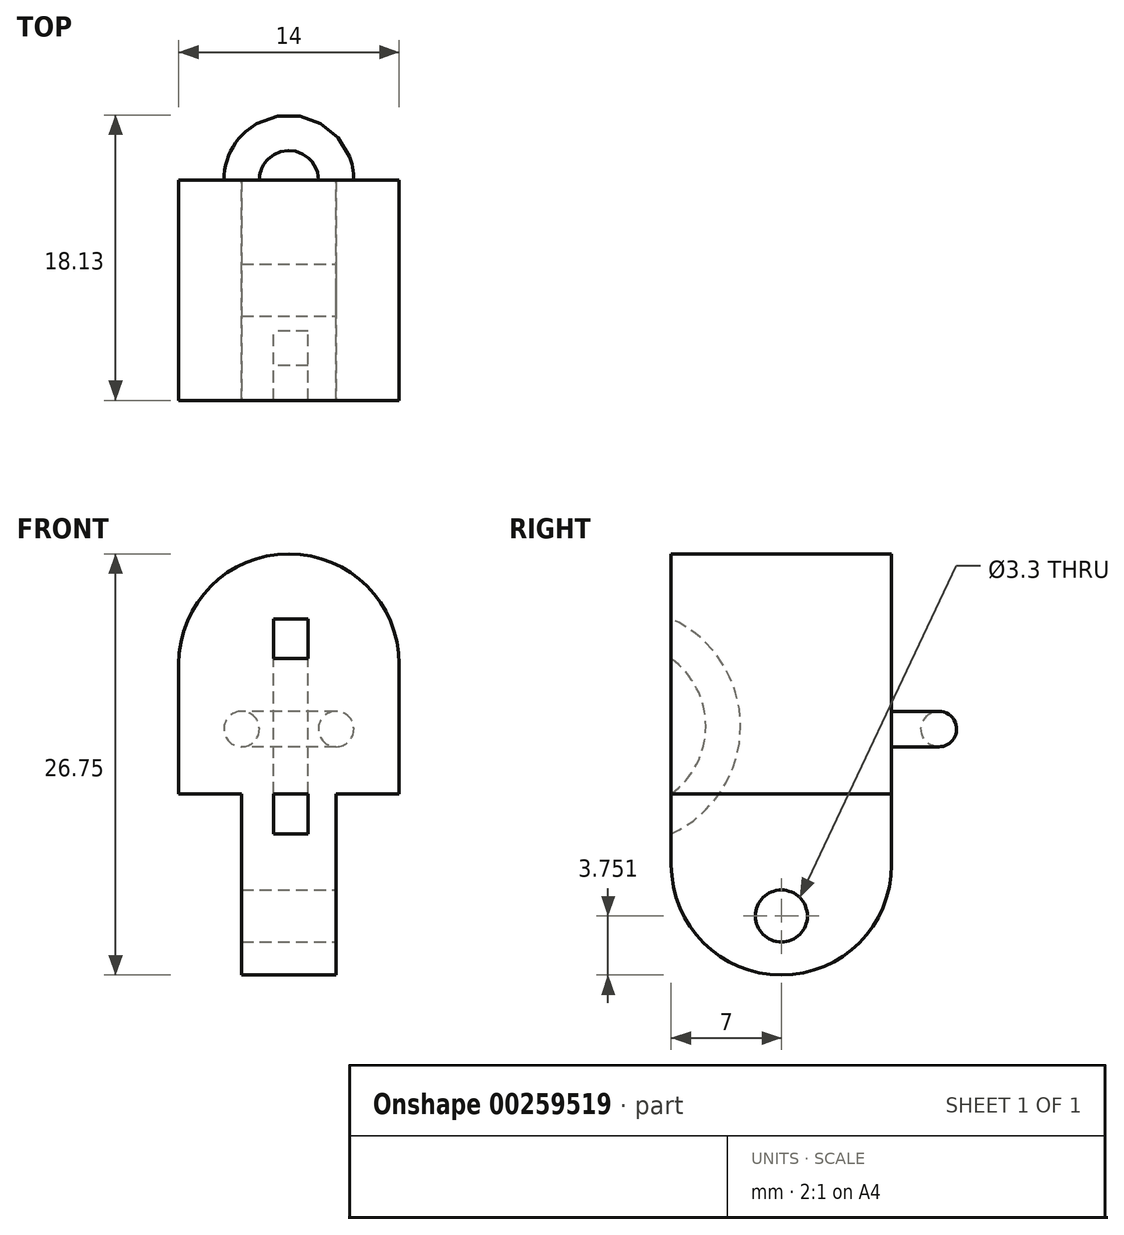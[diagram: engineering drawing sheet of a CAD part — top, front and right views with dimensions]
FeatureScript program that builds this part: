
annotation { "Feature Type Name" : "Feature", "Feature Type Description" : "" }
export const myFeature = defineFeature(function(context is Context, id is Id, definition is map)
    precondition{}
    {
        {
            var Q0;
            Q0=qCreatedBy(makeId("Front.planeOp"),FACE);
            var sketch = newSketch(context, id + "F0", { "sketchPlane" : qUnion([Q0])});
            skLineSegment(sketch, "E0.left", {"start": v(-38.61, 31.27) * mm, "end": v(-38.61, 23.02) * mm});
            skLineSegment(sketch, "E0.right", {"start": v(-24.61, 31.27) * mm, "end": v(-24.61, 23.02) * mm});
            skArc(sketch, "E1", {"start": v(-24.61, 31.27) * mm, "mid": v(-31.61, 38.27) * mm, "end": v(-38.61, 31.27) * mm});
            skLineSegment(sketch, "E2", {"start": v(-34.61, 19.02) * mm, "end": v(-34.61, 11.52) * mm});
            skLineSegment(sketch, "E3", {"start": v(-34.61, 11.52) * mm, "end": v(-28.61, 11.52) * mm});
            skLineSegment(sketch, "E4", {"start": v(-28.61, 11.52) * mm, "end": v(-28.61, 19.02) * mm});
            skLineSegment(sketch, "E5", {"start": v(-28.61, 11.52) * mm, "end": v(-28.61, 15.27) * mm});
            skPoint(sketch, "E6", {"position": v(-31.61, 38.27) * mm});
            skLineSegment(sketch, "E7", {"start": v(-34.61, 19.02) * mm, "end": v(-34.61, 22.02) * mm});
            skLineSegment(sketch, "E8", {"start": v(-28.61, 19.02) * mm, "end": v(-28.61, 22.02) * mm});
            skLineSegment(sketch, "E9", {"start": v(-34.61, 22.02) * mm, "end": v(-34.61, 23.02) * mm});
            skLineSegment(sketch, "E10", {"start": v(-34.61, 23.02) * mm, "end": v(-38.61, 23.02) * mm});
            skLineSegment(sketch, "E11", {"start": v(-28.61, 22.02) * mm, "end": v(-28.61, 23.02) * mm});
            skLineSegment(sketch, "E12", {"start": v(-28.61, 23.02) * mm, "end": v(-24.61, 23.02) * mm});
            skSolve(sketch);
        }
        {
            var Q0;
            Q0 = qSketchRegion(id + "F0", true);
            extrude(context, id + "F1", {"entities" : qUnion([Q0]), "depth" : 14 * mm});
        }
        {
            var Q0;
            Q0=makeQuery(id+"F1.opExtrude","SWEPT_FACE",FACE,{"disambiguationData":[OSD([sQuery(id+"F0.wireOp",EDGE,"E4")])]});
            var sketch = newSketch(context, id + "F2", { "sketchPlane" : qUnion([Q0])});
            skCircle(sketch, "E13", {"center": v(-7, 15.27) * mm, "radius": 1.65 * mm});
            skSolve(sketch);
        }
        {
            var Q0;
            Q0 = qSketchRegion(id + "F2", true);
            extrude(context, id + "F3", {"entities" : qUnion([Q0]), "operationType" : NewBodyOperationType.REMOVE, "oppositeDirection" : true, "depth" : 25 * mm});
        }
        {
            var Q0;
            Q0=makeQuery(id+"F1.opExtrude","CAP_EDGE",EDGE,{"disambiguationData":[OSD([sQuery(id+"F0.wireOp",EDGE,"E3")])],"isStart":false});
            var Q1;
            Q1=makeQuery(id+"F1.opExtrude","CAP_EDGE",EDGE,{"disambiguationData":[OSD([sQuery(id+"F0.wireOp",EDGE,"E3")])],"isStart":true});
            fillet(context, id + "F4", {"entities" : qUnion([Q0, Q1]), "radius" : 7 * mm, "tangentPropagation" : true, "allowEdgeOverflow" : false});
        }
        {
            var Q0;
            Q0=makeQuery(id+"F1.opExtrude","CAP_FACE",FACE,{"disambiguationData":[OSD([sQuery(id+"F0.wireOp",EDGE,"E0.left"),sQuery(id+"F0.wireOp",EDGE,"E0.right"),sQuery(id+"F0.wireOp",EDGE,"E1"),sQuery(id+"F0.wireOp",EDGE,"E2"),sQuery(id+"F0.wireOp",EDGE,"E3"),sQuery(id+"F0.wireOp",EDGE,"E4"),sQuery(id+"F0.wireOp",EDGE,"E5"),sQuery(id+"F0.wireOp",EDGE,"E7"),sQuery(id+"F0.wireOp",EDGE,"E8"),sQuery(id+"F0.wireOp",EDGE,"E9"),sQuery(id+"F0.wireOp",EDGE,"E10"),sQuery(id+"F0.wireOp",EDGE,"E11"),sQuery(id+"F0.wireOp",EDGE,"E12")])],"isStart":false});
            var sketch = newSketch(context, id + "F5", { "sketchPlane" : qUnion([Q0])});
            skLineSegment(sketch, "E14", {"start": v(-31.61, 38.27) * mm, "end": v(-31.61, 18.52) * mm});
            skCircle(sketch, "E15", {"center": v(-34.61, 27.15) * mm, "radius": 1.13 * mm});
            skPoint(sketch, "E16.orphan", {"position": v(-24.61, 27.15) * mm});
            skPoint(sketch, "E17.orphan", {"position": v(-31.61, 27.15) * mm});
            skPoint(sketch, "E18.start.orphan", {"position": v(-38.61, 27.15) * mm});
            skSolve(sketch);
        }
        {
            var Q0;
            Q0=makeQuery(id+"F5.imprint","IMPRINT",FACE,{"disambiguationData":[TD([[makeQuery(id+"F5.imprint","IMPRINT",EDGE,{"derivedFrom":sQuery(id+"F5.wireOp",EDGE,"E15")}),1.0]])]});
            var Q1;
            Q1=sQuery(id+"F5.wireOp",EDGE,"E14");
            revolve(context, id + "F6", {"operationType" : NewBodyOperationType.ADD, "entities" : qUnion([Q0]), "axis" : qUnion([Q1]), "revolveType" : RevolveType.FULL});
        }
        {
            var Q0;
            Q0=makeQuery(id+"F1.opExtrude","CAP_FACE",FACE,{"disambiguationData":[OSD([sQuery(id+"F0.wireOp",EDGE,"E0.left"),sQuery(id+"F0.wireOp",EDGE,"E0.right"),sQuery(id+"F0.wireOp",EDGE,"E1"),sQuery(id+"F0.wireOp",EDGE,"E2"),sQuery(id+"F0.wireOp",EDGE,"E3"),sQuery(id+"F0.wireOp",EDGE,"E4"),sQuery(id+"F0.wireOp",EDGE,"E5"),sQuery(id+"F0.wireOp",EDGE,"E7"),sQuery(id+"F0.wireOp",EDGE,"E8"),sQuery(id+"F0.wireOp",EDGE,"E9"),sQuery(id+"F0.wireOp",EDGE,"E10"),sQuery(id+"F0.wireOp",EDGE,"E11"),sQuery(id+"F0.wireOp",EDGE,"E12")])],"isStart":true});
            var sketch = newSketch(context, id + "F7", { "sketchPlane" : qUnion([Q0])});
            skLineSegment(sketch, "E19", {"start": v(31.61, 38.27) * mm, "end": v(31.61, 18.52) * mm});
            skPoint(sketch, "E20.orphan", {"position": v(38.61, 27.15) * mm});
            skPoint(sketch, "E21.orphan", {"position": v(24.61, 27.15) * mm});
            skCircle(sketch, "E22", {"center": v(28.61, 27.15) * mm, "radius": 1.13 * mm});
            skPoint(sketch, "E23.orphan", {"position": v(31.61, 27.15) * mm});
            skSolve(sketch);
        }
        {
            var Q0;
            Q0=makeQuery(id+"F7.imprint","IMPRINT",FACE,{"disambiguationData":[TD([[makeQuery(id+"F7.imprint","IMPRINT",EDGE,{"derivedFrom":sQuery(id+"F7.wireOp",EDGE,"E22")}),1.0]])]});
            var Q1;
            Q1=sQuery(id+"F7.wireOp",EDGE,"E19");
            revolve(context, id + "F8", {"operationType" : NewBodyOperationType.ADD, "entities" : qUnion([Q0]), "axis" : qUnion([Q1]), "revolveType" : RevolveType.FULL});
        }
        {
            var Q0;
            Q0=qCreatedBy(makeId("Top.planeOp"),FACE);
            var sketch = newSketch(context, id + "F9", { "sketchPlane" : qUnion([Q0])});
            skLineSegment(sketch, "E24.0.0", {"start": v(-24.61, 0) * mm, "end": v(-38.61, 0) * mm});
            skLineSegment(sketch, "E24.0.1", {"start": v(-38.61, 0) * mm, "end": v(-38.61, -14) * mm});
            skLineSegment(sketch, "E24.0.2", {"start": v(-38.61, -14) * mm, "end": v(-24.61, -14) * mm});
            skLineSegment(sketch, "E24.0.3", {"start": v(-24.61, -14) * mm, "end": v(-24.61, 0) * mm});
            skLineSegment(sketch, "E25.top", {"start": v(-38.61, -20.43) * mm, "end": v(-24.61, -20.43) * mm});
            skLineSegment(sketch, "E25.left", {"start": v(-38.61, -14) * mm, "end": v(-38.61, -20.43) * mm});
            skLineSegment(sketch, "E25.right", {"start": v(-24.61, -14) * mm, "end": v(-24.61, -20.43) * mm});
            skSolve(sketch);
        }
        {
            var Q0;
            Q0=makeQuery(id+"F9.imprint","IMPRINT",FACE,{"disambiguationData":[TD([[makeQuery(id+"F9.imprint","IMPRINT",EDGE,{"derivedFrom":sQuery(id+"F9.wireOp",EDGE,"E24.0.2")}),-1.0]])]});
            extrude(context, id + "F10", {"entities" : qUnion([Q0]), "operationType" : NewBodyOperationType.REMOVE, "depth" : 29.7 * mm});
        }
        {
            var Q0;
            Q0=qCreatedBy(makeId("Right.planeOp"),FACE);
            cPlane(context, id + "F11", {"entities" : qUnion([Q0]), "cplaneType" : CPlaneType.OFFSET, "offset" : 31.5 * mm, "oppositeDirection" : true, "width" : 150 * mm, "height" : 150 * mm});
        }
        {
            var Q0;
            Q0=qCreatedBy(id+"F11.planeOp",FACE);
            var sketch = newSketch(context, id + "F12", { "sketchPlane" : qUnion([Q0])});
            skArc(sketch, "E26", {"start": v(-14, 23.03) * mm, "mid": v(-11.8, 27.32) * mm, "end": v(-14, 31.62) * mm});
            skArc(sketch, "E27", {"start": v(-14, 20.5) * mm, "mid": v(-9.6, 27.32) * mm, "end": v(-14, 34.15) * mm});
            skLineSegment(sketch, "E28", {"start": v(-14, 34.15) * mm, "end": v(-14, 31.62) * mm});
            skPoint(sketch, "E29.orphan", {"position": v(-14, 18.52) * mm});
            skLineSegment(sketch, "E30.trimOffspring", {"start": v(-14, 23.03) * mm, "end": v(-14, 20.5) * mm});
            skPoint(sketch, "E31.orphan", {"position": v(-14, 38.27) * mm});
            skSolve(sketch);
        }
        {
            var Q0;
            Q0 = qSketchRegion(id + "F12", true);
            extrude(context, id + "F13", {"entities" : qUnion([Q0]), "operationType" : NewBodyOperationType.REMOVE, "endBound" : BoundingType.SYMMETRIC, "depth" : 2.2 * mm});
        }
    });
